FREECAD ASSEMBLY — COMPONENT RECIPES ("assembly")

This assembly document has 19 components, labeled P0..P18 below (a component is one placed body or linked part). 0 of them carry a construction recipe — the FreeCAD feature program that regenerates the part from scratch, quoted from this document or its linked companion documents; the rest are supplied as boundary geometry only. No exploded tour is included for this assembly.
COMPONENT P0 — geometry summary ("glass"; no construction recipe available for this part):
  bounding box: 600.0 x 585.2 x 216.2 mm
  tessellated surface: 348 triangles
  volume: 2231698 mm^3 (3% of its bounding box)
  symmetry: 2-fold rotationally symmetric about the y axis; mirror-symmetric across its y mid-plane
COMPONENT P1 — geometry summary ("control_panel"; no construction recipe available for this part):
  bounding box: 600.0 x 200.1 x 43.1 mm
  tessellated surface: 7,068 triangles
  volume: 1659194 mm^3 (32% of its bounding box)
COMPONENT P2 — geometry summary ("back_top_door"; no construction recipe available for this part):
  bounding box: 600.0 x 460.0 x 15.0 mm
  tessellated surface: 12 triangles
  volume: 4140000 mm^3 (100% of its bounding box)
  symmetry: 2-fold rotationally symmetric about the y axis; mirror-symmetric across its z mid-plane
COMPONENT P3 — geometry summary ("back_subwoffer_door"; no construction recipe available for this part):
  bounding box: 600.0 x 290.0 x 15.0 mm
  tessellated surface: 12 triangles
  volume: 2610000 mm^3 (100% of its bounding box)
  symmetry: 2-fold rotationally symmetric about the x axis; 2-fold rotationally symmetric about the y axis; 2-fold rotationally symmetric about the z axis; mirror-symmetric across its x mid-plane, y mid-plane, z mid-plane
COMPONENT P4 — geometry summary ("back_bottom_door"; no construction recipe available for this part):
  bounding box: 600.0 x 430.0 x 15.0 mm
  tessellated surface: 12 triangles
  volume: 3870000 mm^3 (100% of its bounding box)
  symmetry: 2-fold rotationally symmetric about the x axis; 2-fold rotationally symmetric about the y axis; 2-fold rotationally symmetric about the z axis; mirror-symmetric across its x mid-plane, z mid-plane
COMPONENT P5 — geometry summary ("bottom"; no construction recipe available for this part):
  bounding box: 600.0 x 380.0 x 15.0 mm
  tessellated surface: 12 triangles
  volume: 3420000 mm^3 (100% of its bounding box)
  symmetry: 2-fold rotationally symmetric about the y axis; 2-fold rotationally symmetric about the z axis; mirror-symmetric across its x mid-plane, y mid-plane, z mid-plane
COMPONENT P6 — geometry summary ("subwoofer_top"; no construction recipe available for this part):
  bounding box: 600.0 x 380.0 x 15.0 mm
  tessellated surface: 12 triangles
  volume: 3420000 mm^3 (100% of its bounding box)
  symmetry: 2-fold rotationally symmetric about the y axis; 2-fold rotationally symmetric about the z axis; mirror-symmetric across its x mid-plane, y mid-plane, z mid-plane
COMPONENT P7 — geometry summary ("connector_panel"; no construction recipe available for this part):
  bounding box: 600.0 x 300.0 x 15.0 mm
  tessellated surface: 1,952 triangles
  volume: 2652697 mm^3 (98% of its bounding box)
  symmetry: 2-fold rotationally symmetric about the z axis; mirror-symmetric across its x mid-plane, y mid-plane
COMPONENT P8 — geometry summary ("ctrl_panel_front"; no construction recipe available for this part):
  bounding box: 600.0 x 120.9 x 31.8 mm
  tessellated surface: 1,068 triangles
  volume: 1026847 mm^3 (44% of its bounding box)
COMPONENT P9 — geometry summary ("ctrl_panel_bottom"; no construction recipe available for this part):
  bounding box: 600.0 x 140.0 x 15.0 mm
  tessellated surface: 972 triangles
  volume: 1246428 mm^3 (99% of its bounding box)
  symmetry: 2-fold rotationally symmetric about the x axis; mirror-symmetric across its y mid-plane
COMPONENT P10 — geometry summary ("fan_plane"; no construction recipe available for this part):
  bounding box: 600.0 x 137.9 x 137.9 mm
  tessellated surface: 1,028 triangles
  volume: 1280708 mm^3 (11% of its bounding box)
  symmetry: 2-fold rotationally symmetric about the y axis; mirror-symmetric across its y mid-plane
COMPONENT P11 — geometry summary ("front"; no construction recipe available for this part):
  bounding box: 850.0 x 600.0 x 15.0 mm
  tessellated surface: 12 triangles
  volume: 7650000 mm^3 (100% of its bounding box)
  symmetry: 2-fold rotationally symmetric about the x axis; mirror-symmetric across its y mid-plane, z mid-plane
COMPONENT P12 — geometry summary ("internal_plate"; no construction recipe available for this part):
  bounding box: 600.0 x 220.0 x 15.0 mm
  tessellated surface: 12 triangles
  volume: 1980000 mm^3 (100% of its bounding box)
  symmetry: 2-fold rotationally symmetric about the x axis; 2-fold rotationally symmetric about the y axis; 2-fold rotationally symmetric about the z axis; mirror-symmetric across its y mid-plane, z mid-plane
COMPONENT P13 — geometry summary ("internal_separator"; no construction recipe available for this part):
  bounding box: 600.0 x 500.0 x 15.0 mm
  tessellated surface: 12 triangles
  volume: 4500000 mm^3 (100% of its bounding box)
  symmetry: 2-fold rotationally symmetric about the x axis; 2-fold rotationally symmetric about the y axis; 2-fold rotationally symmetric about the z axis; mirror-symmetric across its x mid-plane, y mid-plane, z mid-plane
COMPONENT P14 — geometry summary ("marquee"; no construction recipe available for this part):
  bounding box: 600.0 x 167.7 x 37.9 mm
  tessellated surface: 196 triangles
  volume: 999141 mm^3 (26% of its bounding box)
  symmetry: 2-fold rotationally symmetric about the y axis; mirror-symmetric across its y mid-plane
COMPONENT P15 — geometry summary ("side_left"; no construction recipe available for this part):
  bounding box: 1700.0 x 586.7 x 16.0 mm
  tessellated surface: 1,228 triangles
  volume: 11375333 mm^3 (71% of its bounding box)
  symmetry: mirror-symmetric across its y mid-plane
COMPONENT P16 — geometry summary ("side_right"; no construction recipe available for this part):
  bounding box: 1700.0 x 586.7 x 16.0 mm
  tessellated surface: 1,228 triangles
  volume: 11375333 mm^3 (71% of its bounding box)
  symmetry: mirror-symmetric across its y mid-plane
COMPONENT P17 — geometry summary ("speaker_panel"; no construction recipe available for this part):
  bounding box: 600.0 x 160.2 x 42.6 mm
  tessellated surface: 1,028 triangles
  volume: 1289204 mm^3 (32% of its bounding box)
COMPONENT P18 — geometry summary ("top"; no construction recipe available for this part):
  bounding box: 600.0 x 170.0 x 15.0 mm
  tessellated surface: 12 triangles
  volume: 1530000 mm^3 (100% of its bounding box)
  symmetry: 2-fold rotationally symmetric about the x axis; 2-fold rotationally symmetric about the y axis; mirror-symmetric across its x mid-plane, y mid-plane, z mid-plane
PROVENANCE & LICENSES
A FreeCAD (.FCStd) document from a public repository crawl; recipes are the document's own serialized feature recipes (and, for linked parts, companion documents' recipes).
License: cc-by-sa-4.0.
